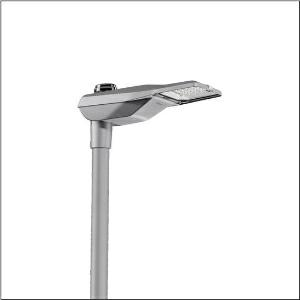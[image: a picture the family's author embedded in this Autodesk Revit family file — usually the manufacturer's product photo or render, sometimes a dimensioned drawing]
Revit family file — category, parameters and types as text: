
# Revit family: streetlight_sl_21_micro___stw1_0a_5xe5e47n08cb_41ee
name_source: partatom
category: Lighting Fixtures
units: mm (PartAtom-declared; Revit-internal decimal feet)

## family parameters
Cut with Voids When Loaded = No
Host = Face
Light Source = No
Part Type = Normal
Room Calculation Point = No
Round Connector Dimension = Use Diameter
Shared = No

## types (1)
- --- (1 x LED, 2380 lm, 15.8 W, 4000K)
    Apparent Load = 16 VA
    CIE Flux Codes = 38 75 98 100 100
    Color Rendering = 70
    Color Temperature = 4000K
    Default Elevation = 1800 mm
    Description = Streetlight SL 21 micro, mast luminaire, primary light control with lens, of PMMA, primary optical cover: cover, of toughened safety glass, transparent, light distribution: STW1.0a, light emission: direct distribution, primary light characteristic: asymmetric, installation type: post-top, LED, 3G 1.5mm², High Power LED, rated luminous flux: 2.380lm, luminous efficacy: 151lm/W, light colour: 740, colour temperature: 4000K, control: overheat protection, pre-setting: linear dimming characteristic, constant luminous flux control, time-dependent luminous flux control, flexible luminous flux parameterisation, mains connection: 230..240V, AC, 50/60Hz, connection cable pre-assembled, cable length: 6,5m, wiring characteristics: H07RN-F, start of lifetime: 16W, end of service life: 16W, reduction: 8W, luminaire housing, of diecast aluminium (EN AC-44300), powder-coated, Siteco® metallic grey (DB 702S), corrosivity category C5 mid according to DIN EN ISO 12944, multi-level sealing system, sealing non-destructively replaceable, inclination adjustable: 0°, 5°, 10°, 15°, length: 528mm, width: 235mm, height: 110mm, spigot size: 76/60mm (post-top), protection rating (complete): IP66, insulation class (complete): insulation class I (protective earthing), certification: CE, ENEC, ENEC+, VDE, impact resistance: IK09, permissible operating ambient temperature for outdoor applications: -40..+50°C, standard-compliant lighting for roads and squares, packaging unit: 1 piece

Light Distribution: STW1.0a
    Height = 110 mm
    Lamp = 1 x LED
    Lamp Light Flux = 2380 lm
    Lamp Power = 15.8 W
    Lamp count = 1
    Length = 528 mm
    Luminous efficacy = 151 lm/W
    Manufacturer = Siteco
    ModVariant = No
    Model = 5XE5E47N08CB
    Number of Poles = 1
    OnlyDefault = Yes
    Power Factor = 1
    Product Name = Streetlight SL 21 micro | STW1.0a
    Product group = mast luminaire | pylon top
    ProductGroupID = 6100
    Protection Class = Protection class I
    Protection Degree = IP 66
    RLX_Detail_Level = 1
    RLX_Emergency_Light_Flux = 0 lm
    RLX_Emergency_Type = 0
    RLX_Emergency_Type_DB = No
    RlxData = <blob elided: 98121 chars, md5=84931209>
    Socket = socket
    Standby Power = 0 W
    System Light Flux = 2380 lm
    System Power = 16 W
    Type Comments = factory setting: luminous flux: 100 % | dim-lin: 254 | 300 mA
    Type Image = l_1294375.jpg
    URL = http://relux.com
    VarID = @adj_105595
    Voltage = 0 V
    Weight = 0.00 kg
    Width = 235 mm

## geometry (parser evidence)
native form markers: Blend x4, Sweep x12
no freeform markers — native parametric forms only
